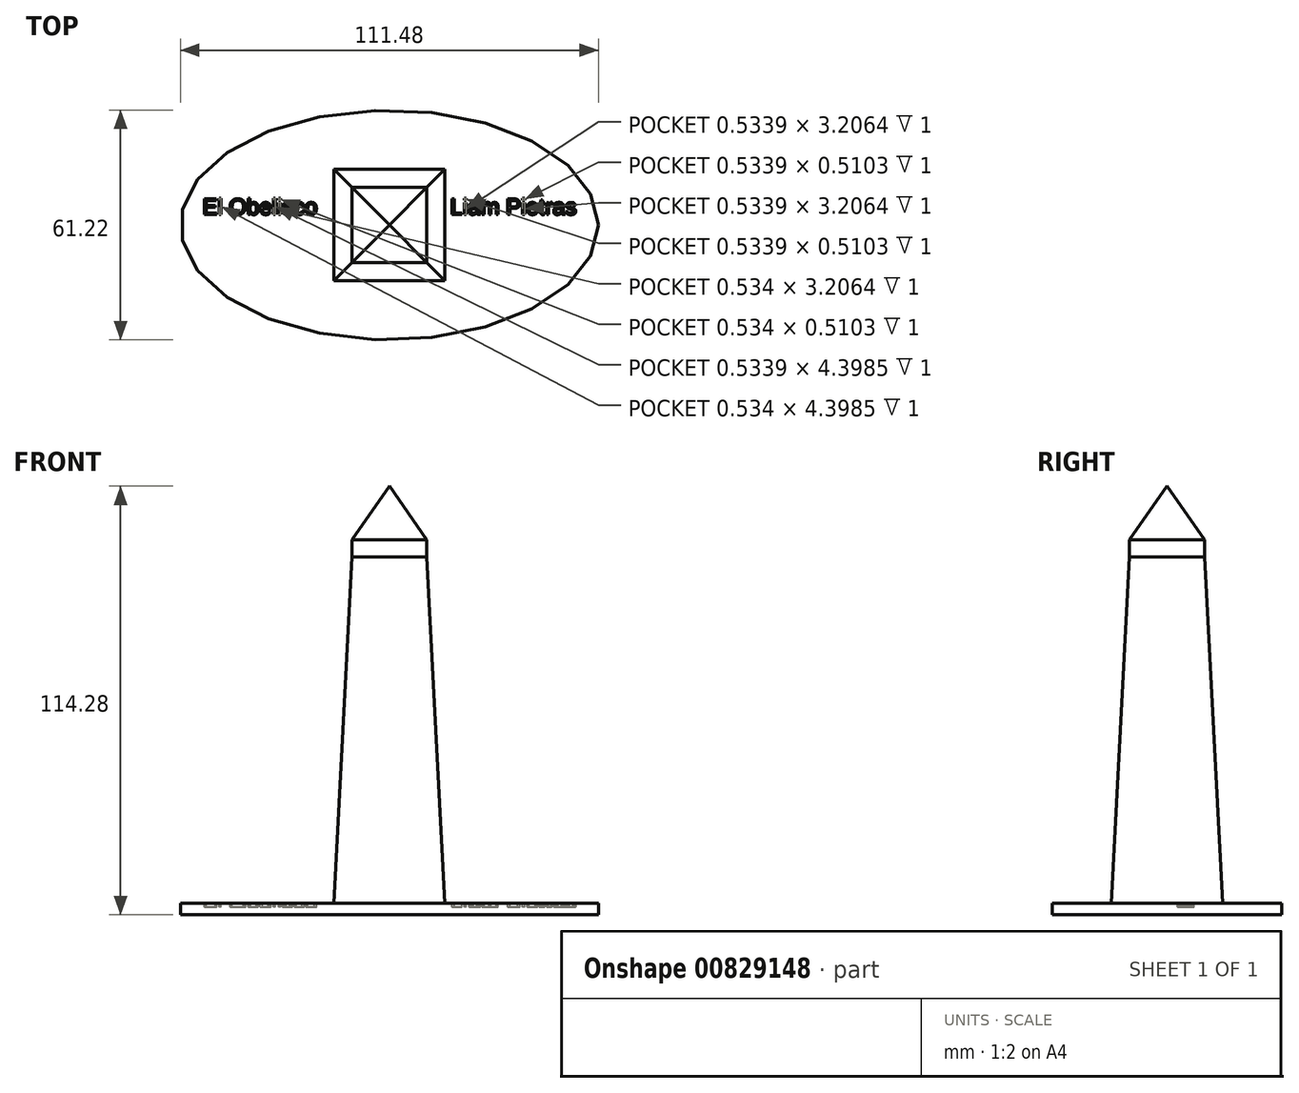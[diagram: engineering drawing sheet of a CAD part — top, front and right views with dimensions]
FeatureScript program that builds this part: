
annotation { "Feature Type Name" : "Feature", "Feature Type Description" : "" }
export const myFeature = defineFeature(function(context is Context, id is Id, definition is map)
    precondition{}
    {
        {
            var Q0;
            Q0=qCreatedBy(makeId("Top.planeOp"),FACE);
            var sketch = newSketch(context, id + "F0", { "sketchPlane" : qUnion([Q0])});
            skLineSegment(sketch, "E0.bottom", {"start": v(-15, 15) * mm, "end": v(15, 15) * mm});
            skLineSegment(sketch, "E0.top", {"start": v(-15, -15) * mm, "end": v(15, -15) * mm});
            skLineSegment(sketch, "E0.left", {"start": v(-15, 15) * mm, "end": v(-15, -15) * mm});
            skLineSegment(sketch, "E0.right", {"start": v(15, 15) * mm, "end": v(15, -15) * mm});
            skPoint(sketch, "E0.middle", {"position": v(0, 0) * mm});
            skSolve(sketch);
        }
        {
            var Q0;
            Q0=qCreatedBy(makeId("Top.planeOp"),FACE);
            cPlane(context, id + "F1", {"entities" : qUnion([Q0]), "cplaneType" : CPlaneType.OFFSET, "offset" : 100 * mm, "width" : 150 * mm, "height" : 150 * mm});
        }
        {
            var Q0;
            Q0=qCreatedBy(id+"F1.planeOp",FACE);
            var sketch = newSketch(context, id + "F2", { "sketchPlane" : qUnion([Q0])});
            skLineSegment(sketch, "E1.bottom", {"start": v(-10, 10) * mm, "end": v(10, 10) * mm});
            skLineSegment(sketch, "E1.top", {"start": v(-10, -10) * mm, "end": v(10, -10) * mm});
            skLineSegment(sketch, "E1.left", {"start": v(-10, 10) * mm, "end": v(-10, -10) * mm});
            skLineSegment(sketch, "E1.right", {"start": v(10, 10) * mm, "end": v(10, -10) * mm});
            skPoint(sketch, "E1.middle", {"position": v(0, 0) * mm});
            skSolve(sketch);
        }
        {
            var Q0;
            Q0=makeQuery(id+"F0.imprint","IMPRINT",FACE,{"disambiguationData":[TD([[makeQuery(id+"F0.imprint","IMPRINT",EDGE,{"derivedFrom":sQuery(id+"F0.wireOp",EDGE,"E0.bottom")}),-1.0]])]});
            var Q1;
            Q1=qCreatedBy(id+"F1.planeOp",FACE);
            extrude(context, id + "F3", {"entities" : qUnion([Q0]), "endBound" : BoundingType.UP_TO_SURFACE, "depth" : 25 * mm, "endBoundEntityFace" : qUnion([Q1]), "offsetDistance" : 25 * mm, "hasDraft" : true, "draftAngle" : 3 * degree, "draftPullDirection" : true});
        }
        {
            var Q0;
            Q0=makeQuery(id+"F2.imprint","IMPRINT",FACE,{"disambiguationData":[TD([[makeQuery(id+"F2.imprint","IMPRINT",EDGE,{"derivedFrom":sQuery(id+"F2.wireOp",EDGE,"E1.bottom")}),-1.0]])]});
            extrude(context, id + "F4", {"entities" : qUnion([Q0]), "operationType" : NewBodyOperationType.ADD, "depth" : 15 * mm, "offsetDistance" : 25 * mm, "hasDraft" : true, "draftAngle" : 35 * degree, "draftPullDirection" : true, "hasSecondDirection" : true, "secondDirectionOppositeDirection" : true, "secondDirectionDepth" : 25 * mm});
        }
        {
            var Q0;
            Q0=qCreatedBy(makeId("Top.planeOp"),FACE);
            var sketch = newSketch(context, id + "F5", { "sketchPlane" : qUnion([Q0])});
            skEllipse(sketch, "E2", {"center": v(0, 0) * mm, "majorRadius": 55.74 * mm, "minorRadius": 30.61 * mm, "majorAxis": v(1, 0)});
            skSolve(sketch);
        }
        {
            var Q0;
            Q0=makeQuery(id+"F5.imprint","IMPRINT",FACE,{"disambiguationData":[TD([[makeQuery(id+"F5.imprint","IMPRINT",EDGE,{"derivedFrom":sQuery(id+"F5.wireOp",EDGE,"E2")}),1.0]])]});
            extrude(context, id + "F6", {"entities" : qUnion([Q0]), "operationType" : NewBodyOperationType.ADD, "depth" : 3 * mm, "offsetDistance" : 25 * mm});
        }
        {
            var Q0;
            Q0=makeQuery(id+"F6.opExtrude","CAP_FACE",FACE,{"disambiguationData":[OSD([sQuery(id+"F5.wireOp",EDGE,"E2")])],"isStart":false});
            var sketch = newSketch(context, id + "F7", { "sketchPlane" : qUnion([Q0])});
            skText(sketch, "E3", { "text": "El Obelisco                     Liam Pietras\n", "fontName": "Arimo-Regular.ttf"});
            const initialGuessF7  = {"E3": [-0.04988, 0.00278, 1, 0, 0.00437]};
            skSetInitialGuess(sketch, initialGuessF7);
            skSolve(sketch);
        }
        {
            var Q0;
            Q0 = qSketchRegion(id + "F7", true);
            extrude(context, id + "F8", {"entities" : qUnion([Q0]), "operationType" : NewBodyOperationType.REMOVE, "oppositeDirection" : true, "depth" : 1 * mm, "offsetDistance" : 25 * mm});
        }
    });
